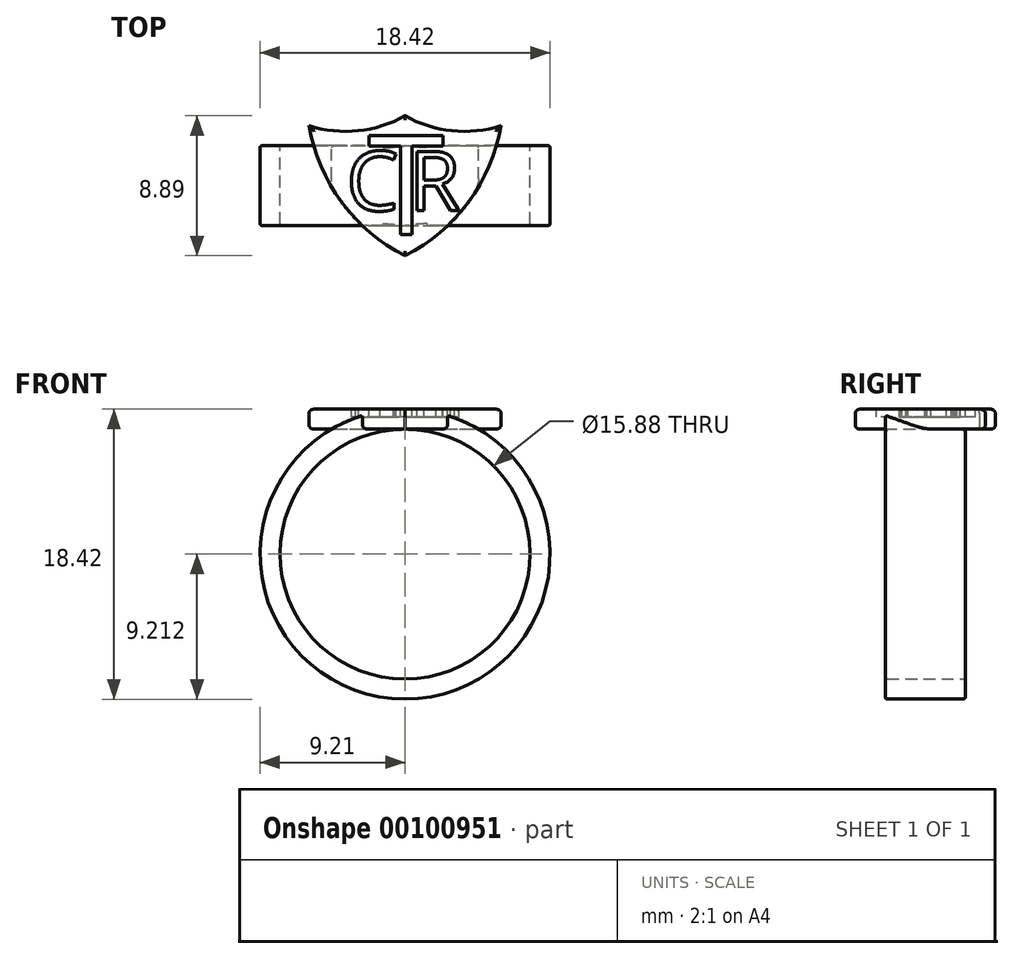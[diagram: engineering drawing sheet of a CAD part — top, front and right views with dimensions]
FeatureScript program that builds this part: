
annotation { "Feature Type Name" : "Feature", "Feature Type Description" : "" }
export const myFeature = defineFeature(function(context is Context, id is Id, definition is map)
    precondition{}
    {
        {
            var Q0;
            Q0=qCreatedBy(makeId("Top.planeOp"),FACE);
            var sketch = newSketch(context, id + "F0", { "sketchPlane" : qUnion([Q0])});
            skLineSegment(sketch, "E0", {"start": v(0, 0) * mm, "end": v(9.52, 0) * mm, "construction": true});
            skLineSegment(sketch, "E1", {"start": v(9.53, 0) * mm, "end": v(9.53, -8.9) * mm, "construction": true});
            skLineSegment(sketch, "E2", {"start": v(9.52, -8.89) * mm, "end": v(-9.52, -8.9) * mm, "construction": true});
            skLineSegment(sketch, "E3", {"start": v(-9.52, -8.9) * mm, "end": v(-9.52, 0) * mm, "construction": true});
            skLineSegment(sketch, "E4", {"start": v(-9.52, 0) * mm, "end": v(0, 0) * mm, "construction": true});
            skArc(sketch, "E5", {"start": v(-6.1, -0.63) * mm, "mid": v(-4.03, -5.49) * mm, "end": v(0, -8.89) * mm});
            skArc(sketch, "E6", {"start": v(-6.1, -0.64) * mm, "mid": v(-2.98, -0.96) * mm, "end": v(0, 0) * mm});
            skArc(sketch, "E7.MirrorCS", {"start": v(6.1, -0.64) * mm, "mid": v(2.98, -0.96) * mm, "end": v(0, 0) * mm});
            skArc(sketch, "E8.MirrorCS", {"start": v(6.1, -0.63) * mm, "mid": v(4.03, -5.49) * mm, "end": v(0, -8.89) * mm});
            skSolve(sketch);
        }
        {
            var Q0;
            Q0=qSketchRegion(id+"F0",true);
            extrude(context, id + "F1", {"entities" : qUnion([Q0]), "depth" : 1.27 * mm});
        }
        {
            var Q0;
            Q0=qCreatedBy(makeId("Right.planeOp"),FACE);
            var sketch = newSketch(context, id + "F2", { "sketchPlane" : qUnion([Q0])});
            skLineSegment(sketch, "E9.bottom", {"start": v(-1.9, 0) * mm, "end": v(-6.98, 0) * mm});
            skLineSegment(sketch, "E9.top", {"start": v(-1.9, 1.27) * mm, "end": v(-6.98, 1.27) * mm});
            skLineSegment(sketch, "E9.left", {"start": v(-1.9, 1.27) * mm, "end": v(-1.9, 0) * mm});
            skLineSegment(sketch, "E9.right", {"start": v(-6.98, 1.27) * mm, "end": v(-6.98, 0) * mm});
            skLineSegment(sketch, "E10", {"start": v(0, 0) * mm, "end": v(-8.89, 0) * mm, "construction": true});
            skLineSegment(sketch, "E11", {"start": v(-4.44, 0) * mm, "end": v(-4.44, 3.33) * mm, "construction": true});
            skLineSegment(sketch, "E12", {"start": v(2.72, -7.94) * mm, "end": v(-10.6, -7.94) * mm, "construction": true});
            skLineSegment(sketch, "E13.0", {"start": v(-8.89, 1.27) * mm, "end": v(-8.89, 0) * mm, "construction": true});
            skSolve(sketch);
        }
        {
            var Q0;
            Q0=qSketchRegion(id+"F2",true);
            var Q1;
            Q1=sQuery(id+"F2.wireOp",EDGE,"E12");
            revolve(context, id + "F3", {"operationType" : NewBodyOperationType.ADD, "entities" : qUnion([Q0]), "axis" : qUnion([Q1]), "revolveType" : RevolveType.FULL});
        }
        {
            var Q0;
            Q0=makeQuery(id+"F3.opRevolve","SWEPT_EDGE",EDGE,{"disambiguationData":[OSD([sQuery(id+"F2.wireOp",EDGE,"E9.top"),sQuery(id+"F2.wireOp",EDGE,"E9.right")])]});
            var Q1;
            Q1=makeQuery(id+"F3.opRevolve","SWEPT_EDGE",EDGE,{"disambiguationData":[OSD([sQuery(id+"F2.wireOp",EDGE,"E9.bottom"),sQuery(id+"F2.wireOp",EDGE,"E9.right")])]});
            var Q2;
            Q2=makeQuery(id+"F3.opRevolve","SWEPT_EDGE",EDGE,{"disambiguationData":[OSD([sQuery(id+"F2.wireOp",EDGE,"E9.top"),sQuery(id+"F2.wireOp",EDGE,"E9.left")])]});
            var Q3;
            Q3=makeQuery(id+"F3.opRevolve","SWEPT_EDGE",EDGE,{"disambiguationData":[OSD([sQuery(id+"F2.wireOp",EDGE,"E9.bottom"),sQuery(id+"F2.wireOp",EDGE,"E9.left")])]});
            fillet(context, id + "F4", {"entities" : qUnion([Q0, Q1, Q2, Q3]), "radius" : 0.13 * mm, "tangentPropagation" : true, "allowEdgeOverflow" : false});
        }
        {
            var Q0;
            Q0=makeQuery(id+"F1.opExtrude","CAP_FACE",FACE,{"disambiguationData":[OSD([sQuery(id+"F0.wireOp",EDGE,"dtAdijCY-2Pwo-jMmh-0q7I-SGrLHdXILtFh"),sQuery(id+"F0.wireOp",EDGE,"E5"),sQuery(id+"F0.wireOp",EDGE,"b53439b5-4433-4b26-adde-5d4ad1fb86ac0.MirrorCS"),sQuery(id+"F0.wireOp",EDGE,"ad21d0f8-95ba-4c56-aa77-77bde63a10fc0.MirrorCS")])],"isStart":false});
            var sketch = newSketch(context, id + "F5", { "sketchPlane" : qUnion([Q0])});
            skText(sketch, "E14", { "text": "T", "fontName": "OpenSans-Regular.ttf"});
            skText(sketch, "E15", { "text": "C\n", "fontName": "OpenSans-Regular.ttf"});
            skText(sketch, "E16", { "text": "R", "fontName": "OpenSans-Regular.ttf"});
            const initialGuessF5  = {"E14": [-0.00237, -0.00756, 1, 0, 0.00635], "E15": [-0.00373, -0.00603, 1, 0, 0.0038], "E16": [0.00024, -0.00603, 1, 0, 0.0038]};
            skSetInitialGuess(sketch, initialGuessF5);
            skSolve(sketch);
        }
        {
            var Q0;
            Q0=qSketchRegion(id+"F5",true);
            extrude(context, id + "F6", {"entities" : qUnion([Q0]), "operationType" : NewBodyOperationType.REMOVE, "oppositeDirection" : true, "depth" : 0.5 * mm});
        }
        {
            var Q0;
            {var subQ0=sQuery(id+"F0.wireOp",EDGE,"ad21d0f8-95ba-4c56-aa77-77bde63a10fc0.MirrorCS");var subQ1=sQuery(id+"F0.wireOp",EDGE,"b53439b5-4433-4b26-adde-5d4ad1fb86ac0.MirrorCS");Q0=makeQuery(id+"F3.boolean.opBoolean","SPLIT",EDGE,{"disambiguationData":[TD([makeQuery(id+"F1.opExtrude","SWEPT_FACE",FACE,{"disambiguationData":[OSD([subQ1])]})])],"derivedFrom":makeQuery(id+"F1.opExtrude","CAP_EDGE",EDGE,{"disambiguationData":[OSD([subQ0])],"isStart":true})});}
            var Q1;
            {var subQ0=sQuery(id+"F0.wireOp",EDGE,"ad21d0f8-95ba-4c56-aa77-77bde63a10fc0.MirrorCS");var subQ1=sQuery(id+"F0.wireOp",EDGE,"E5");Q1=makeQuery(id+"F3.boolean.opBoolean","SPLIT",EDGE,{"disambiguationData":[TD([makeQuery(id+"F1.opExtrude","SWEPT_FACE",FACE,{"disambiguationData":[OSD([subQ1])]})])],"derivedFrom":makeQuery(id+"F1.opExtrude","CAP_EDGE",EDGE,{"disambiguationData":[OSD([subQ0])],"isStart":true})});}
            var Q2;
            {var subQ0=sQuery(id+"F0.wireOp",EDGE,"ad21d0f8-95ba-4c56-aa77-77bde63a10fc0.MirrorCS");var subQ1=sQuery(id+"F0.wireOp",EDGE,"E5");Q2=makeQuery(id+"F3.boolean.opBoolean","SPLIT",EDGE,{"disambiguationData":[TD([makeQuery(id+"F1.opExtrude","SWEPT_FACE",FACE,{"disambiguationData":[OSD([subQ0])]})])],"derivedFrom":makeQuery(id+"F1.opExtrude","CAP_EDGE",EDGE,{"disambiguationData":[OSD([subQ1])],"isStart":true})});}
            var Q3;
            {var subQ0=sQuery(id+"F0.wireOp",EDGE,"dtAdijCY-2Pwo-jMmh-0q7I-SGrLHdXILtFh");var subQ1=sQuery(id+"F0.wireOp",EDGE,"E5");Q3=makeQuery(id+"F3.boolean.opBoolean","SPLIT",EDGE,{"disambiguationData":[TD([makeQuery(id+"F1.opExtrude","SWEPT_FACE",FACE,{"disambiguationData":[OSD([subQ0])]})])],"derivedFrom":makeQuery(id+"F1.opExtrude","CAP_EDGE",EDGE,{"disambiguationData":[OSD([subQ1])],"isStart":true})});}
            var Q4;
            Q4=makeQuery(id+"F1.opExtrude","CAP_EDGE",EDGE,{"disambiguationData":[OSD([sQuery(id+"F0.wireOp",EDGE,"dtAdijCY-2Pwo-jMmh-0q7I-SGrLHdXILtFh")])],"isStart":true});
            var Q5;
            Q5=makeQuery(id+"F1.opExtrude","CAP_EDGE",EDGE,{"disambiguationData":[OSD([sQuery(id+"F0.wireOp",EDGE,"b53439b5-4433-4b26-adde-5d4ad1fb86ac0.MirrorCS")])],"isStart":true});
            var Q6;
            Q6=makeQuery(id+"F1.opExtrude","CAP_EDGE",EDGE,{"disambiguationData":[OSD([sQuery(id+"F0.wireOp",EDGE,"dtAdijCY-2Pwo-jMmh-0q7I-SGrLHdXILtFh")])],"isStart":false});
            var Q7;
            Q7=makeQuery(id+"F1.opExtrude","CAP_EDGE",EDGE,{"disambiguationData":[OSD([sQuery(id+"F0.wireOp",EDGE,"E5")])],"isStart":false});
            var Q8;
            Q8=makeQuery(id+"F1.opExtrude","CAP_EDGE",EDGE,{"disambiguationData":[OSD([sQuery(id+"F0.wireOp",EDGE,"ad21d0f8-95ba-4c56-aa77-77bde63a10fc0.MirrorCS")])],"isStart":false});
            var Q9;
            Q9=makeQuery(id+"F1.opExtrude","CAP_EDGE",EDGE,{"disambiguationData":[OSD([sQuery(id+"F0.wireOp",EDGE,"b53439b5-4433-4b26-adde-5d4ad1fb86ac0.MirrorCS")])],"isStart":false});
            var Q10;
            Q10=makeQuery(id+"F1.opExtrude","CAP_EDGE",EDGE,{"disambiguationData":[OSD([sQuery(id+"F0.wireOp",EDGE,"E6")])],"isStart":false});
            var Q11;
            Q11=makeQuery(id+"F1.opExtrude","CAP_EDGE",EDGE,{"disambiguationData":[OSD([sQuery(id+"F0.wireOp",EDGE,"E7.MirrorCS")])],"isStart":false});
            var Q12;
            Q12=makeQuery(id+"F1.opExtrude","CAP_EDGE",EDGE,{"disambiguationData":[OSD([sQuery(id+"F0.wireOp",EDGE,"E8.MirrorCS")])],"isStart":false});
            var Q13;
            {var subQ0=sQuery(id+"F0.wireOp",EDGE,"E8.MirrorCS");var subQ1=sQuery(id+"F0.wireOp",EDGE,"E7.MirrorCS");Q13=makeQuery(id+"F3.boolean.opBoolean","SPLIT",EDGE,{"disambiguationData":[TD([makeQuery(id+"F1.opExtrude","SWEPT_FACE",FACE,{"disambiguationData":[OSD([subQ1])]})])],"derivedFrom":makeQuery(id+"F1.opExtrude","CAP_EDGE",EDGE,{"disambiguationData":[OSD([subQ0])],"isStart":true})});}
            var Q14;
            {var subQ0=sQuery(id+"F0.wireOp",EDGE,"E5");var subQ1=sQuery(id+"F0.wireOp",EDGE,"E8.MirrorCS");Q14=makeQuery(id+"F3.boolean.opBoolean","SPLIT",EDGE,{"disambiguationData":[TD([makeQuery(id+"F1.opExtrude","SWEPT_FACE",FACE,{"disambiguationData":[OSD([subQ0])]})])],"derivedFrom":makeQuery(id+"F1.opExtrude","CAP_EDGE",EDGE,{"disambiguationData":[OSD([subQ1])],"isStart":true})});}
            var Q15;
            {var subQ0=sQuery(id+"F0.wireOp",EDGE,"E5");var subQ1=sQuery(id+"F0.wireOp",EDGE,"E8.MirrorCS");Q15=makeQuery(id+"F3.boolean.opBoolean","SPLIT",EDGE,{"disambiguationData":[TD([makeQuery(id+"F1.opExtrude","SWEPT_FACE",FACE,{"disambiguationData":[OSD([subQ1])]})])],"derivedFrom":makeQuery(id+"F1.opExtrude","CAP_EDGE",EDGE,{"disambiguationData":[OSD([subQ0])],"isStart":true})});}
            var Q16;
            {var subQ0=sQuery(id+"F0.wireOp",EDGE,"E5");var subQ1=sQuery(id+"F0.wireOp",EDGE,"E6");Q16=makeQuery(id+"F3.boolean.opBoolean","SPLIT",EDGE,{"disambiguationData":[TD([makeQuery(id+"F1.opExtrude","SWEPT_FACE",FACE,{"disambiguationData":[OSD([subQ1])]})])],"derivedFrom":makeQuery(id+"F1.opExtrude","CAP_EDGE",EDGE,{"disambiguationData":[OSD([subQ0])],"isStart":true})});}
            var Q17;
            Q17=makeQuery(id+"F1.opExtrude","CAP_EDGE",EDGE,{"disambiguationData":[OSD([sQuery(id+"F0.wireOp",EDGE,"E6")])],"isStart":true});
            var Q18;
            Q18=makeQuery(id+"F1.opExtrude","CAP_EDGE",EDGE,{"disambiguationData":[OSD([sQuery(id+"F0.wireOp",EDGE,"E7.MirrorCS")])],"isStart":true});
            fillet(context, id + "F7", {"entities" : qUnion([Q0, Q1, Q2, Q3, Q4, Q5, Q6, Q7, Q8, Q9, Q10, Q11, Q12, Q13, Q14, Q15, Q16, Q17, Q18]), "radius" : 0.25 * mm, "tangentPropagation" : true, "allowEdgeOverflow" : false});
        }
    });
